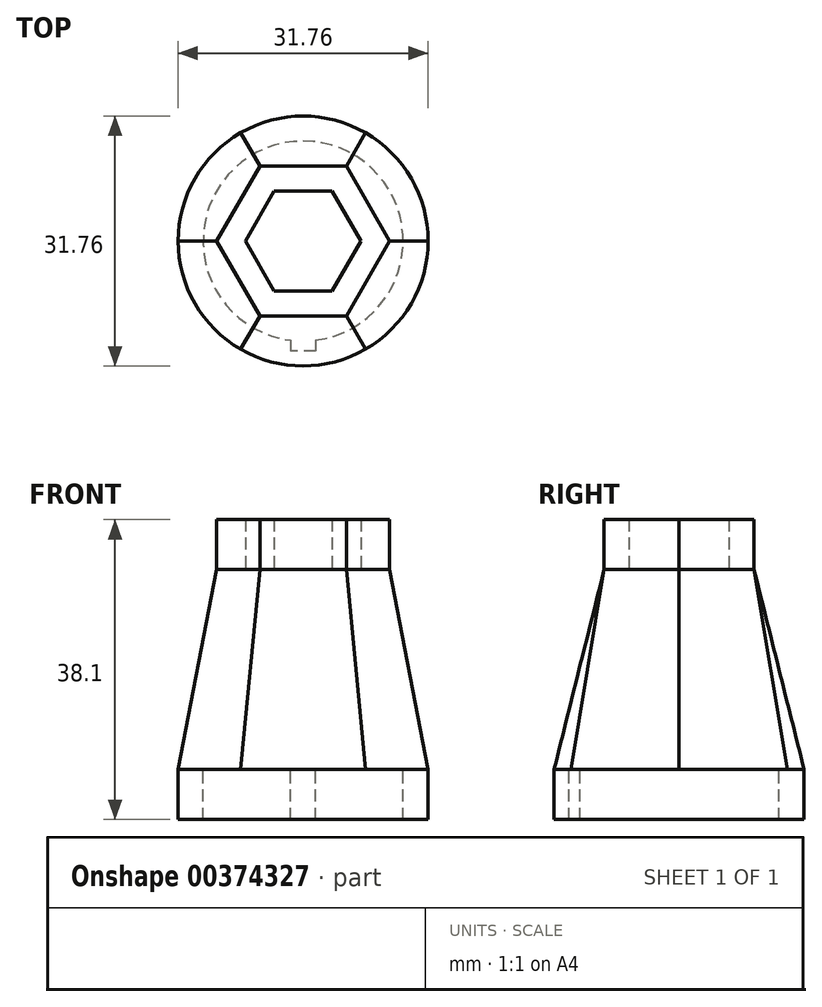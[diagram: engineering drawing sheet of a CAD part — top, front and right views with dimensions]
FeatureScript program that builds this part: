
annotation { "Feature Type Name" : "Feature", "Feature Type Description" : "" }
export const myFeature = defineFeature(function(context is Context, id is Id, definition is map)
    precondition{}
    {
        {
            var Q0;
            Q0=qCreatedBy(makeId("Top.planeOp"),FACE);
            cPlane(context, id + "F0", {"entities" : qUnion([Q0]), "cplaneType" : CPlaneType.OFFSET, "offset" : 25.4 * mm, "width" : 152.4 * mm, "height" : 152.4 * mm});
        }
        {
            var Q0;
            Q0=qCreatedBy(id+"F0.planeOp",FACE);
            var sketch = newSketch(context, id + "F1", { "sketchPlane" : qUnion([Q0])});
            skCircle(sketch, "E0.cCircle", {"center": v(0, 0) * mm, "radius": 9.53 * mm, "construction": true});
            skLineSegment(sketch, "E0.0", {"start": v(5.5, 9.52) * mm, "end": v(11, 0) * mm});
            skLineSegment(sketch, "E0.1", {"start": v(11, 0) * mm, "end": v(5.5, -9.53) * mm});
            skLineSegment(sketch, "E0.2", {"start": v(5.5, -9.52) * mm, "end": v(-5.5, -9.52) * mm});
            skLineSegment(sketch, "E0.3", {"start": v(-5.5, -9.52) * mm, "end": v(-11, 0) * mm});
            skLineSegment(sketch, "E0.4", {"start": v(-11, 0) * mm, "end": v(-5.5, 9.53) * mm});
            skLineSegment(sketch, "E0.5", {"start": v(-5.5, 9.52) * mm, "end": v(5.5, 9.52) * mm});
            skPoint(sketch, "E0.0.midPoint", {"position": v(8.25, 4.76) * mm});
            skLineSegment(sketch, "E1.0", {"start": v(-7.33, 0) * mm, "end": v(-3.67, 6.35) * mm});
            skLineSegment(sketch, "E1.1", {"start": v(3.67, 6.35) * mm, "end": v(7.33, 0) * mm});
            skLineSegment(sketch, "E1.2", {"start": v(7.33, 0) * mm, "end": v(3.67, -6.35) * mm});
            skLineSegment(sketch, "E1.3", {"start": v(-3.67, 6.35) * mm, "end": v(3.67, 6.35) * mm});
            skLineSegment(sketch, "E1.4", {"start": v(3.67, -6.35) * mm, "end": v(-3.67, -6.35) * mm});
            skLineSegment(sketch, "E1.5", {"start": v(-3.67, -6.35) * mm, "end": v(-7.33, 0) * mm});
            skSolve(sketch);
        }
        {
            var Q0;
            Q0=qCreatedBy(makeId("Top.planeOp"),FACE);
            var sketch = newSketch(context, id + "F2", { "sketchPlane" : qUnion([Q0])});
            skCircle(sketch, "E2", {"center": v(0, 0) * mm, "radius": 15.88 * mm});
            skCircle(sketch, "E3", {"center": v(0, 0) * mm, "radius": 12.7 * mm});
            skLineSegment(sketch, "E4.top", {"start": v(1.59, -13.97) * mm, "end": v(-1.59, -13.97) * mm});
            skLineSegment(sketch, "E4.left", {"start": v(1.59, -12.6) * mm, "end": v(1.59, -13.97) * mm});
            skLineSegment(sketch, "E4.right", {"start": v(-1.59, -12.6) * mm, "end": v(-1.59, -13.97) * mm});
            skPoint(sketch, "E4.middle", {"position": v(0, -12.7) * mm});
            skLineSegment(sketch, "E5", {"start": v(0, -14.92) * mm, "end": v(0, 0) * mm, "construction": true});
            skPoint(sketch, "E6", {"position": v(0, -13.97) * mm});
            skSolve(sketch);
        }
        {
            var Q0;
            Q0 = qSketchRegion(id + "F1", true);
            extrude(context, id + "F3", {"entities" : qUnion([Q0]), "depth" : 6.35 * mm});
        }
        {
            var Q0;
            Q0=makeQuery(id+"F3.opExtrude","CAP_FACE",FACE,{"disambiguationData":[OSD([sQuery(id+"F1.wireOp",EDGE,"E0.0"),sQuery(id+"F1.wireOp",EDGE,"E0.1"),sQuery(id+"F1.wireOp",EDGE,"E0.2"),sQuery(id+"F1.wireOp",EDGE,"E0.3"),sQuery(id+"F1.wireOp",EDGE,"E0.4"),sQuery(id+"F1.wireOp",EDGE,"E0.5"),sQuery(id+"F1.wireOp",EDGE,"E1.0"),sQuery(id+"F1.wireOp",EDGE,"E1.1"),sQuery(id+"F1.wireOp",EDGE,"E1.2"),sQuery(id+"F1.wireOp",EDGE,"E1.3"),sQuery(id+"F1.wireOp",EDGE,"E1.4"),sQuery(id+"F1.wireOp",EDGE,"E1.5")])],"isStart":true});
            var sketch = newSketch(context, id + "F4", { "sketchPlane" : qUnion([Q0])});
            skCircle(sketch, "E7.cCircle", {"center": v(0, 0) * mm, "radius": 9.52 * mm, "construction": true});
            skLineSegment(sketch, "E7.0", {"start": v(-5.5, 9.52) * mm, "end": v(5.5, 9.52) * mm});
            skLineSegment(sketch, "E7.1", {"start": v(5.5, 9.52) * mm, "end": v(11, 0) * mm});
            skLineSegment(sketch, "E7.2", {"start": v(11, 0) * mm, "end": v(5.5, -9.52) * mm});
            skLineSegment(sketch, "E7.3", {"start": v(5.5, -9.52) * mm, "end": v(-5.5, -9.52) * mm});
            skLineSegment(sketch, "E7.4", {"start": v(-5.5, -9.52) * mm, "end": v(-11, 0) * mm});
            skLineSegment(sketch, "E7.5", {"start": v(-11, 0) * mm, "end": v(-5.5, 9.52) * mm});
            skPoint(sketch, "E7.0.midPoint", {"position": v(0, 9.52) * mm});
            skSolve(sketch);
        }
        {
            var Q0;
            Q0=qCreatedBy(makeId("Top.planeOp"),FACE);
            var sketch = newSketch(context, id + "F5", { "sketchPlane" : qUnion([Q0])});
            skCircle(sketch, "E8.0", {"center": v(0, 0) * mm, "radius": 15.88 * mm});
            skSolve(sketch);
        }
        {
            var Q1;
            Q1 = qSketchRegion(id + "F4", true);
            var Q2;
            Q2 = qSketchRegion(id + "F5", true);
            loft(context, id + "F6", {"operationType" : NewBodyOperationType.ADD, "sheetProfilesArray" : [{ "sheetProfileEntities" : qUnion([Q1]) }, { "sheetProfileEntities" : qUnion([Q2]) }]});
        }
        {
            var Q0;
            Q0=makeQuery(id+"F2.imprint","IMPRINT",FACE,{"disambiguationData":[TD([[makeQuery(id+"F2.imprint","IMPRINT",EDGE,{"derivedFrom":sQuery(id+"F2.wireOp",EDGE,"E2")}),1.0]])]});
            extrude(context, id + "F7", {"entities" : qUnion([Q0]), "operationType" : NewBodyOperationType.ADD, "oppositeDirection" : true, "depth" : 6.35 * mm});
        }
    });
